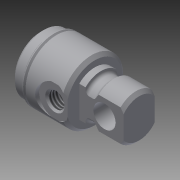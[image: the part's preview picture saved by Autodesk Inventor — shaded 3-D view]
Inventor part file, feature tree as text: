
AUTODESK INVENTOR PART (.ipt)
format: ipt  version: 2014 SP2 (Build 180246200, 246)  size: 306,688 bytes
history: native  units: in
note: dims shown in document units (in); Inventor stores cm internally (conversion verified against a paired STEP export)
features: other x154, sketch x7, revolve x4, extrude x2, hole x1, thread x1
ambient origin geometry x8: Origin, YZ Plane, XZ Plane, XY Plane, X Axis, Y Axis, Z Axis, Center Point
bodies: Solid1 (feature_tree)
feature tree (169):
  revolve  "Revolution1"  Angle=360.0deg
  revolve  "Revolution2"  Angle=360.0deg
  extrude  "Extrusion1"  TaperAngle=360.0deg  [1 undecoded]
  hole  "Hole1"  [1 undecoded]
  revolve  "Revolution3"  [1 undecoded]
  thread  "Thread1"  [1 undecoded]
  revolve  "Revolution4"  [1 undecoded]
  extrude  "Extrusion2"  [1 undecoded]
  other  "1_XY"
  other  "1_YZ"
  other  "1_ZX"
  other  "1_X"
  other  "1_Y"
  other  "1_Z"
  other  "1_Center"
  other  "c1_XY"
  other  "c1_YZ"
  other  "c1_ZX"
  other  "c1_X"
  other  "c1_Y"
  other  "c1_Z"
  other  "c1_Center"
  other  "c2_XY"
  other  "c2_YZ"
  other  "c2_ZX"
  other  "c2_X"
  other  "c2_Y"
  other  "c2_Z"
  other  "c2_Center"
  other  "cc1_XY"
  other  "cc1_YZ"
  other  "cc1_ZX"
  other  "cc1_X"
  other  "cc1_Y"
  other  "cc1_Z"
  other  "cc1_Center"
  other  "cc2_XY"
  other  "cc2_YZ"
  other  "cc2_ZX"
  other  "cc2_X"
  other  "cc2_Y"
  other  "cc2_Z"
  other  "cc2_Center"
  other  "lovra1_XY"
  other  "lovra1_YZ"
  other  "lovra1_ZX"
  other  "lovra1_X"
  other  "lovra1_Y"
  other  "lovra1_Z"
  other  "lovra1_Center"
  other  "lovra2_XY"
  other  "lovra2_YZ"
  other  "lovra2_ZX"
  other  "lovra2_X"
  other  "lovra2_Y"
  other  "lovra2_Z"
  other  "lovra2_Center"
  other  "lovra21_XY"
  other  "lovra21_YZ"
  other  "lovra21_ZX"
  other  "lovra21_X"
  other  "lovra21_Y"
  other  "lovra21_Z"
  other  "lovra21_Center"
  other  "lovra22_XY"
  other  "lovra22_YZ"
  other  "lovra22_ZX"
  other  "lovra22_X"
  other  "lovra22_Y"
  other  "lovra22_Z"
  other  "lovra22_Center"
  other  "lovra3_XY"
  other  "lovra3_YZ"
  other  "lovra3_ZX"
  other  "lovra3_X"
  other  "lovra3_Y"
  other  "lovra3_Z"
  other  "lovra3_Center"
  other  "olen_XY"
  other  "olen_YZ"
  other  "olen_ZX"
  other  "olen_X"
  other  "olen_Y"
  other  "olen_Z"
  other  "olen_Center"
  other  "p1_XY"
  other  "p1_YZ"
  other  "p1_ZX"
  other  "p1_X"
  other  "p1_Y"
  other  "p1_Z"
  other  "p1_Center"
  other  "p2_XY"
  other  "p2_YZ"
  other  "p2_ZX"
  other  "p2_X"
  other  "p2_Y"
  other  "p2_Z"
  other  "p2_Center"
  other  "port_XY"
  other  "port_YZ"
  other  "port_ZX"
  other  "port_X"
  other  "port_Y"
  other  "port_Z"
  other  "port_Center"
  other  "port2_XY"
  other  "port2_YZ"
  other  "port2_ZX"
  other  "port2_X"
  other  "port2_Y"
  other  "port2_Z"
  other  "port2_Center"
  other  "thd1_XY"
  other  "thd1_YZ"
  other  "thd1_ZX"
  other  "thd1_X"
  other  "thd1_Y"
  other  "thd1_Z"
  other  "thd1_Center"
  other  "thd2_XY"
  other  "thd2_YZ"
  other  "thd2_ZX"
  other  "thd2_X"
  other  "thd2_Y"
  other  "thd2_Z"
  other  "thd2_Center"
  other  "to_mounting_bracket_XY"
  other  "to_mounting_bracket_YZ"
  other  "to_mounting_bracket_ZX"
  other  "to_mounting_bracket_X"
  other  "to_mounting_bracket_Y"
  other  "to_mounting_bracket_Z"
  other  "to_mounting_bracket_Center"
  other  "to_nut_XY"
  other  "to_nut_YZ"
  other  "to_nut_ZX"
  other  "to_nut_X"
  other  "to_nut_Y"
  other  "to_nut_Z"
  other  "to_nut_Center"
  other  "to_pin_XY"
  other  "to_pin_YZ"
  other  "to_pin_ZX"
  other  "to_pin_X"
  other  "to_pin_Y"
  other  "to_pin_Z"
  other  "to_pin_Center"
  other  "to_screw_XY"
  other  "to_screw_YZ"
  other  "to_screw_ZX"
  other  "to_screw_X"
  other  "to_screw_Y"
  other  "to_screw_Z"
  other  "to_screw_Center"
  other  "to_tube_XY"
  other  "to_tube_YZ"
  other  "to_tube_ZX"
  other  "to_tube_X"
  other  "to_tube_Y"
  other  "to_tube_Z"
  other  "to_tube_Center"
  sketch  "Sketch_18"  dims[d15=0.4605in d16=0.0in]
  sketch  "Sketch_15"  dims[d4=0.154in d5=0.75in d6=0.375in d7=0.25in d8=0.5635in d9=0.484in d10=120.0deg d11=360.0deg]
  sketch  "Sketch_9"  dims[d2=0.437in d3=0.0in]
  sketch  "Sketch4"  dims[d0=360.0deg d1=360.0deg]
  sketch  "Sketch_16"  dims[d12=0.1736in d13=0.0in d14=360.0deg]
  sketch  "Sketch_24"  dims[d17=0.0in d18=0.0in d19=0.0in d20=0.0in d21=0.0in d22=0.0in d23=0.0in]
  sketch  "Sketch_43"
note: 6 required parameter values undecoded (feature->parameter linkage not recoverable at this tier; creation-order binding heuristic only, values carry confidence <= 0.55)
